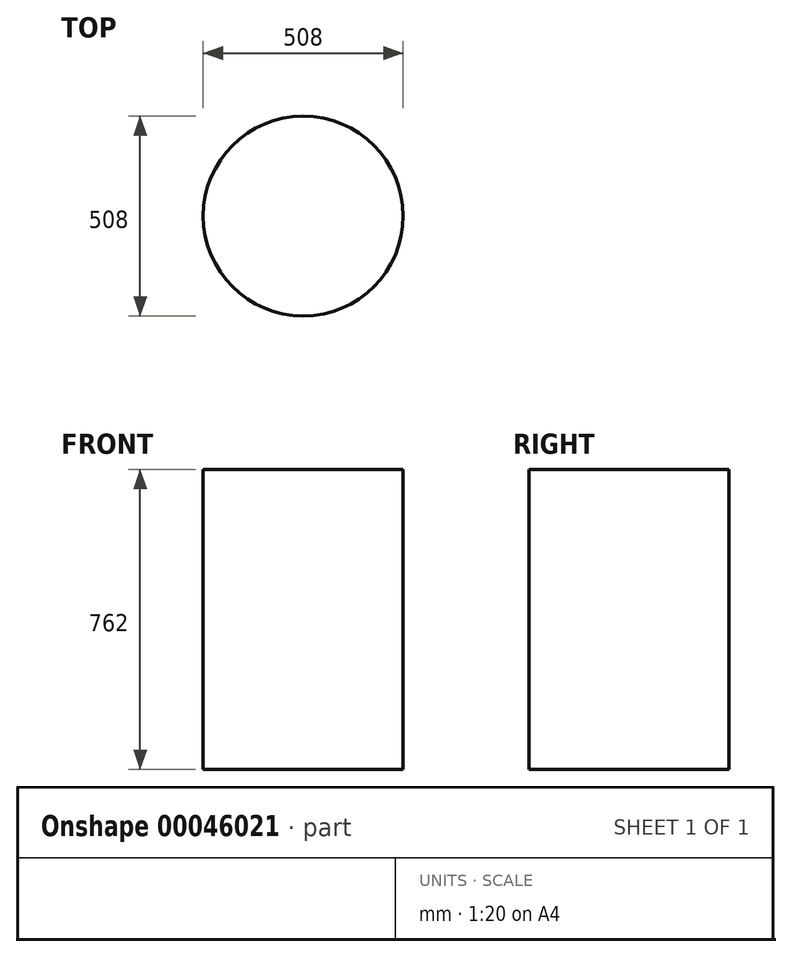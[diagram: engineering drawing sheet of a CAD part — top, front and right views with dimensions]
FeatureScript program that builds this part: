
annotation { "Feature Type Name" : "Feature", "Feature Type Description" : "" }
export const myFeature = defineFeature(function(context is Context, id is Id, definition is map)
    precondition{}
    {
        {
            var Q0;
            Q0=qCreatedBy(makeId("Top.planeOp"),FACE);
            var sketch = newSketch(context, id + "F0", { "sketchPlane" : qUnion([Q0])});
            skCircle(sketch, "E0", {"center": v(0, 0) * mm, "radius": 254 * mm});
            skSolve(sketch);
        }
        {
            var Q0;
            Q0=sQuery(id+"F0.wireOp",EDGE,"E0");
            extrude(context, id + "F1", {"bodyType" : ToolBodyType.SURFACE, "surfaceEntities" : qUnion([Q0]), "depth" : 762 * mm});
        }
    });
